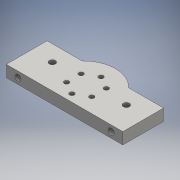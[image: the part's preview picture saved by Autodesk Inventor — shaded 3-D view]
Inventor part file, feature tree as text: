
AUTODESK INVENTOR PART (.ipt)
format: ipt  version: 2016 (Build 200138000, 138)  size: 168,960 bytes
history: native  units: mm
features: other x2, extrude x2, thread x2, sketch x1
ambient origin geometry x8: Origin, YZ Plane, XZ Plane, XY Plane, X Axis, Y Axis, Z Axis, Center Point
bodies: Body1 (feature_tree)
feature tree (7):
  other  "ソリッド1"
  other  "構築線"
  extrude  "押し出し1"  Depth=5.5mm
  extrude  "押し出し3"  Depth=17.0mm
  thread  "ねじ3"
  thread  "ねじ4"
  sketch  "スケッチ5"
